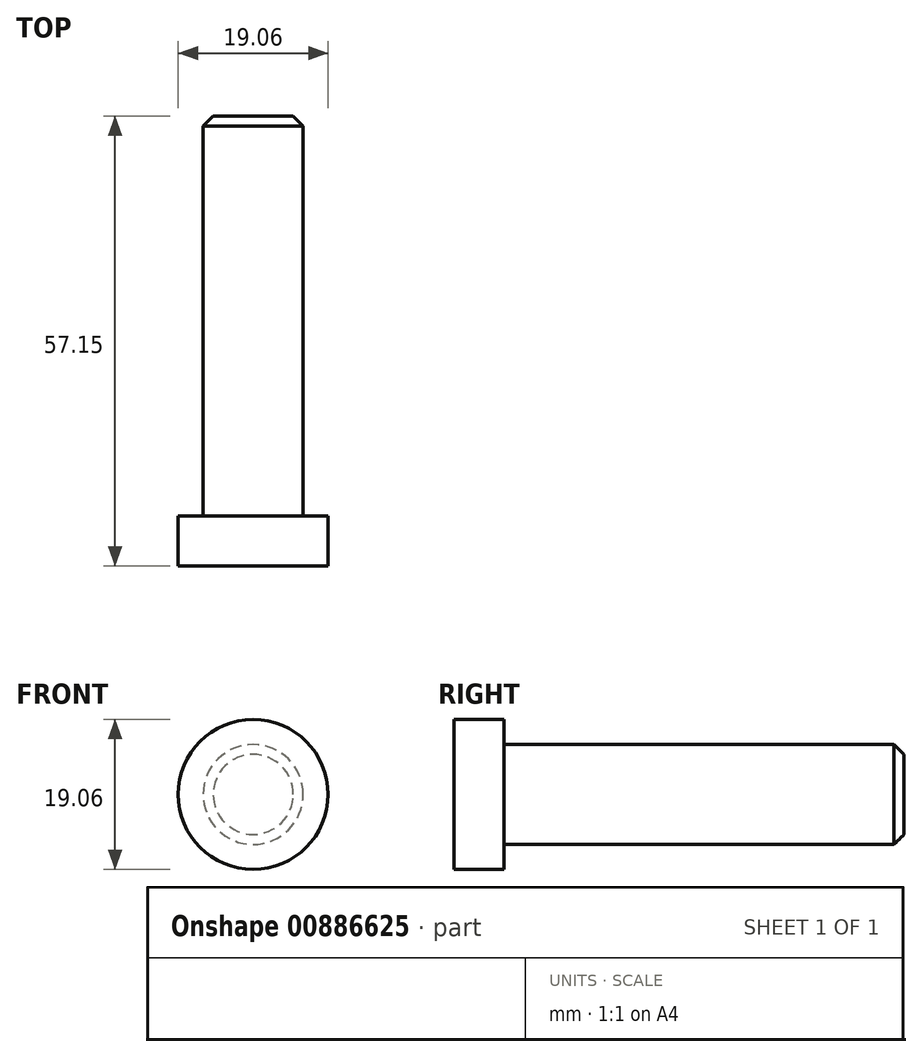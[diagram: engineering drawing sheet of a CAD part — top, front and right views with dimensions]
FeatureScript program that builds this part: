
annotation { "Feature Type Name" : "Feature", "Feature Type Description" : "" }
export const myFeature = defineFeature(function(context is Context, id is Id, definition is map)
    precondition{}
    {
        {
            assignVariable(context, id + "F0", {"name" : "height1", "anyValue" : 50.8 * mm});
        }
        {
            assignVariable(context, id + "F1", {"name" : "height2", "anyValue" : 6.35 * mm});
        }
        {
            var Q0;
            Q0=qCreatedBy(makeId("Front.planeOp"),FACE);
            var sketch = newSketch(context, id + "F2", { "sketchPlane" : qUnion([Q0])});
            skCircle(sketch, "E0", {"center": v(0, 0) * mm, "radius": 9.53 * mm});
            skSolve(sketch);
        }
        {
            var Q0;
            Q0=makeQuery(id+"F2.imprint","IMPRINT",FACE,{"disambiguationData":[TD([[makeQuery(id+"F2.imprint","IMPRINT",EDGE,{"derivedFrom":sQuery(id+"F2.wireOp",EDGE,"E0")}),1.0]])]});
            extrude(context, id + "F3", {"entities" : qUnion([Q0]), "depth" : getVariable(context, 'height2'), "offsetDistance" : 25.4 * mm});
        }
        {
            var Q0;
            Q0=qCreatedBy(makeId("Front.planeOp"),FACE);
            var sketch = newSketch(context, id + "F4", { "sketchPlane" : qUnion([Q0])});
            skCircle(sketch, "E1", {"center": v(0, 0) * mm, "radius": 6.35 * mm});
            skSolve(sketch);
        }
        {
            var Q0;
            Q0=makeQuery(id+"F4.imprint","IMPRINT",FACE,{"disambiguationData":[TD([[makeQuery(id+"F4.imprint","IMPRINT",EDGE,{"derivedFrom":sQuery(id+"F4.wireOp",EDGE,"E1")}),1.0]])]});
            extrude(context, id + "F5", {"entities" : qUnion([Q0]), "operationType" : NewBodyOperationType.ADD, "oppositeDirection" : true, "depth" : getVariable(context, 'height1'), "offsetDistance" : 25.4 * mm});
        }
        {
            var Q0;
            Q0=makeQuery(id+"F5.opExtrude","CAP_EDGE",EDGE,{"disambiguationData":[OSD([sQuery(id+"F4.wireOp",EDGE,"E1")])],"isStart":false});
            chamfer(context, id + "F6", {"entities" : qUnion([Q0]), "width" : 1.27 * mm, "tangentPropagation" : true});
        }
    });
